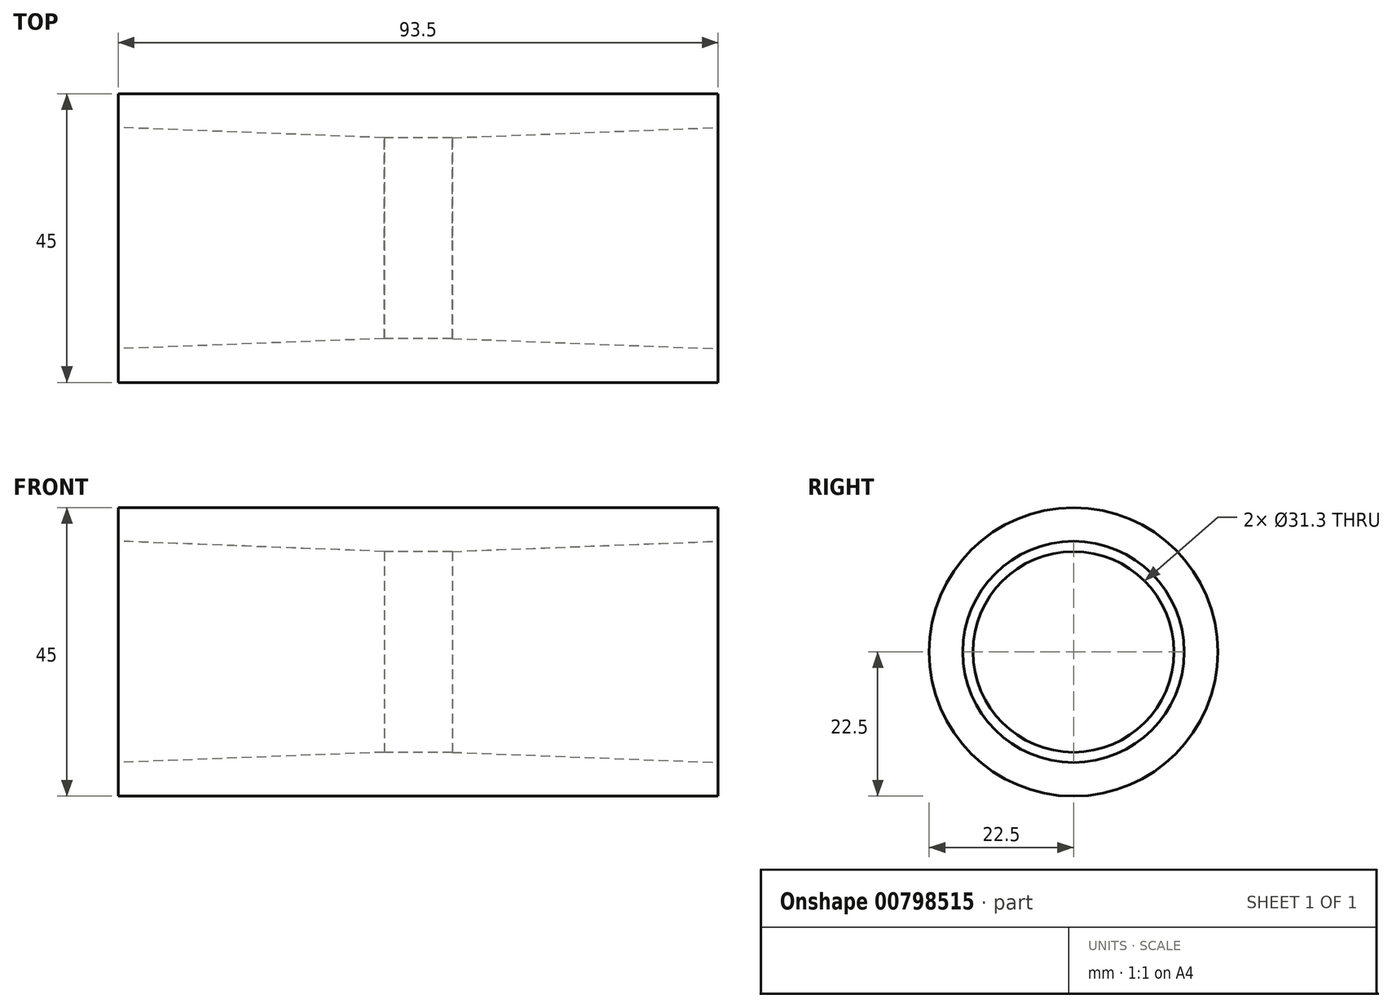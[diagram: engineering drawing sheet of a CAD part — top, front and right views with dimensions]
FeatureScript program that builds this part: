
annotation { "Feature Type Name" : "Feature", "Feature Type Description" : "" }
export const myFeature = defineFeature(function(context is Context, id is Id, definition is map)
    precondition{}
    {
        {
            var Q0;
            Q0=qCreatedBy(makeId("Front.planeOp"),FACE);
            var sketch = newSketch(context, id + "F0", { "sketchPlane" : qUnion([Q0])});
            skLineSegment(sketch, "E0", {"start": v(-99.71, 0) * mm, "end": v(160.53, 0) * mm, "construction": true});
            skLineSegment(sketch, "E1", {"start": v(41.45, 15.65) * mm, "end": v(0, 17.25) * mm});
            skLineSegment(sketch, "E2", {"start": v(0, 17.25) * mm, "end": v(0, 22.5) * mm});
            skLineSegment(sketch, "E3", {"start": v(0, 22.5) * mm, "end": v(46.75, 22.5) * mm});
            skLineSegment(sketch, "E4", {"start": v(41.45, 15.65) * mm, "end": v(46.75, 15.65) * mm});
            skLineSegment(sketch, "E5", {"start": v(46.75, 58.51) * mm, "end": v(46.75, -16.8) * mm, "construction": true});
            skLineSegment(sketch, "E6.MirrorCS", {"start": v(93.5, 17.25) * mm, "end": v(93.5, 22.5) * mm});
            skLineSegment(sketch, "E7.MirrorCS", {"start": v(52.05, 15.65) * mm, "end": v(46.75, 15.65) * mm});
            skLineSegment(sketch, "E8.MirrorCS", {"start": v(93.5, 22.5) * mm, "end": v(46.75, 22.5) * mm});
            skLineSegment(sketch, "E9.MirrorCS", {"start": v(52.05, 15.65) * mm, "end": v(93.5, 17.25) * mm});
            skLineSegment(sketch, "E10.MirrorCS", {"start": v(93.5, -17.25) * mm, "end": v(93.5, -22.5) * mm});
            skLineSegment(sketch, "E11.MirrorCS", {"start": v(0, -17.25) * mm, "end": v(0, -22.5) * mm});
            skLineSegment(sketch, "E12.MirrorCS", {"start": v(41.45, -15.65) * mm, "end": v(46.75, -15.65) * mm});
            skLineSegment(sketch, "E13.MirrorCS", {"start": v(52.05, -15.65) * mm, "end": v(46.75, -15.65) * mm});
            skLineSegment(sketch, "E14.MirrorCS", {"start": v(52.05, -15.65) * mm, "end": v(93.5, -17.25) * mm});
            skLineSegment(sketch, "E15.MirrorCS", {"start": v(93.5, -22.5) * mm, "end": v(46.75, -22.5) * mm});
            skLineSegment(sketch, "E16.MirrorCS", {"start": v(0, -22.5) * mm, "end": v(46.75, -22.5) * mm});
            skLineSegment(sketch, "E17.MirrorCS", {"start": v(41.45, -15.65) * mm, "end": v(0, -17.25) * mm});
            skSolve(sketch);
        }
        {
            var Q0;
            Q0 = qSketchRegion(id + "F0", true);
            var Q1;
            Q1=sQuery(id+"F0.wireOp",EDGE,"E0");
            revolve(context, id + "F1", {"surfaceOperationType" : NewSurfaceOperationType.NEW, "entities" : qUnion([Q0]), "axis" : qUnion([Q1]), "revolveType" : RevolveType.FULL});
        }
    });
